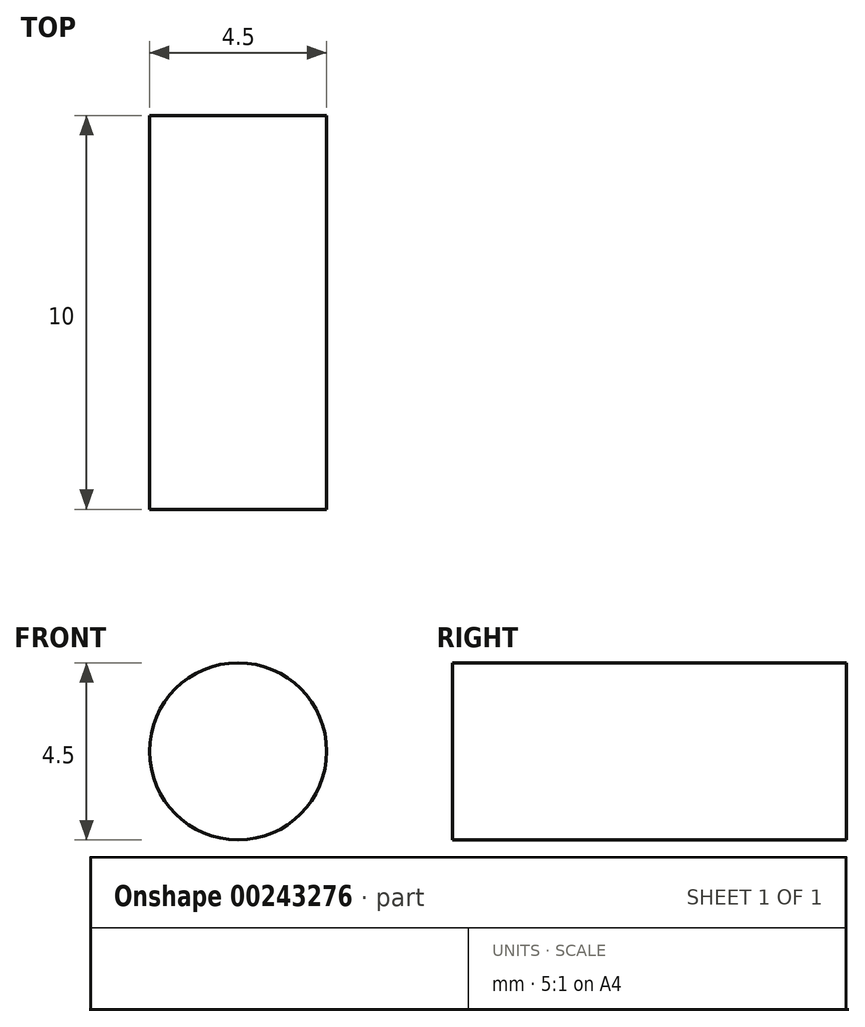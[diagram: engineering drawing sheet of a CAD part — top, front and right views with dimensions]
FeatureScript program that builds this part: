
annotation { "Feature Type Name" : "Feature", "Feature Type Description" : "" }
export const myFeature = defineFeature(function(context is Context, id is Id, definition is map)
    precondition{}
    {
        {
            var Q0;
            Q0=qCreatedBy(makeId("Front.planeOp"),FACE);
            var sketch = newSketch(context, id + "F0", { "sketchPlane" : qUnion([Q0])});
            skCircle(sketch, "E0", {"center": v(0, 0) * mm, "radius": 2.25 * mm});
            skSolve(sketch);
        }
        {
            var Q0;
            Q0=makeQuery(id+"F0.imprint","IMPRINT",FACE,{"disambiguationData":[TD([[makeQuery(id+"F0.imprint","IMPRINT",EDGE,{"derivedFrom":sQuery(id+"F0.wireOp",EDGE,"E0")}),1.0]])]});
            extrude(context, id + "F1", {"entities" : qUnion([Q0]), "depth" : 10 * mm});
        }
    });
